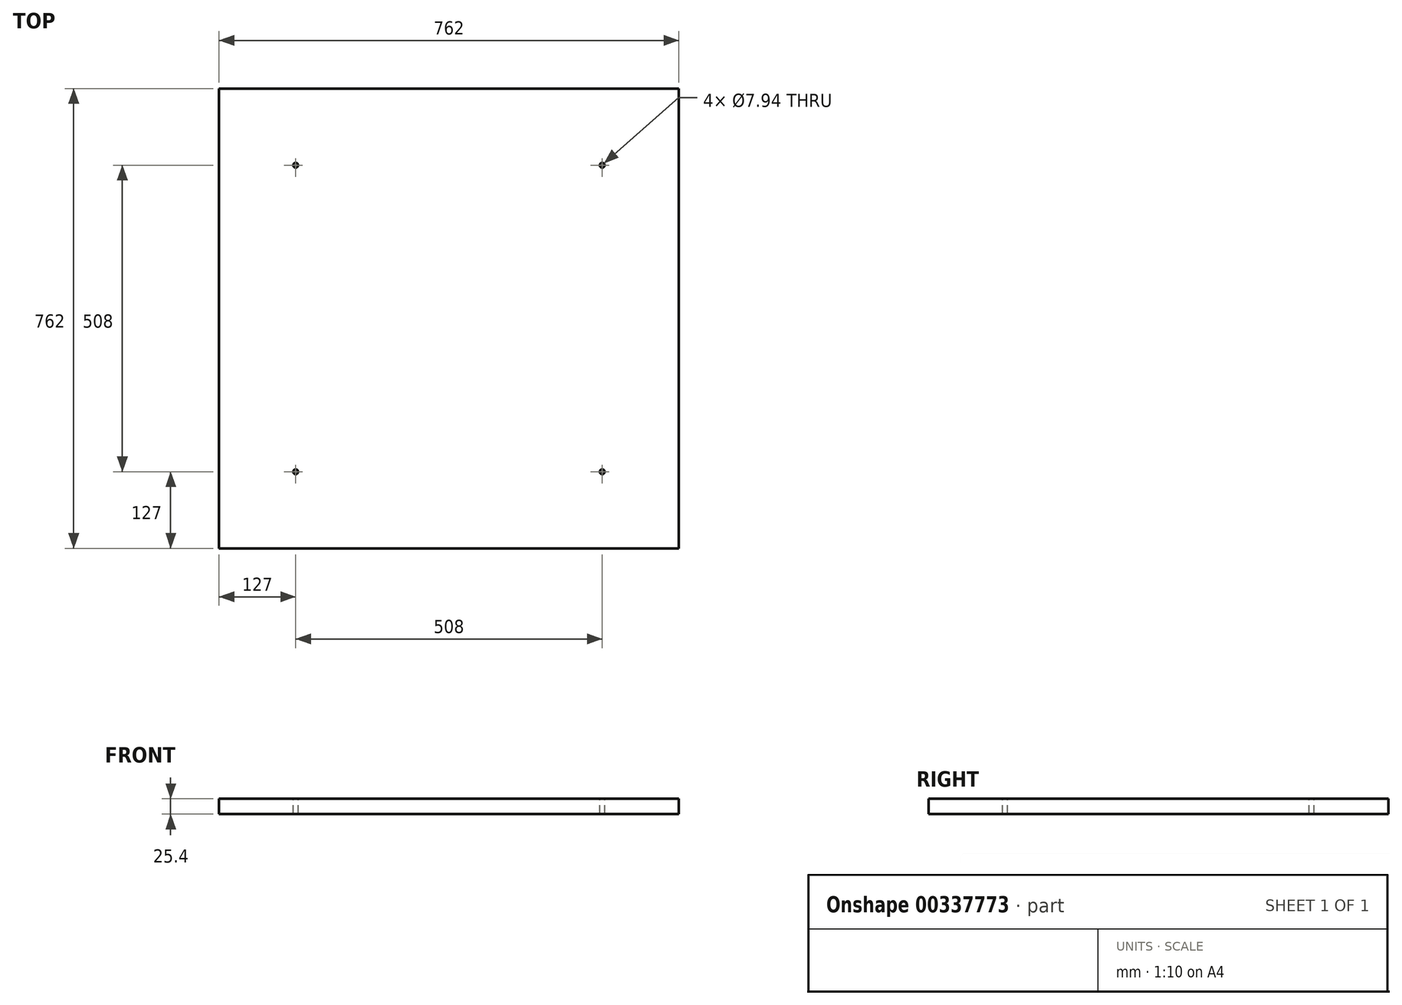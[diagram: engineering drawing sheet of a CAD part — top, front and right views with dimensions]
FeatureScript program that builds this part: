
annotation { "Feature Type Name" : "Feature", "Feature Type Description" : "" }
export const myFeature = defineFeature(function(context is Context, id is Id, definition is map)
    precondition{}
    {
        {
            var Q0;
            Q0=qCreatedBy(makeId("Front.planeOp"),FACE);
            var sketch = newSketch(context, id + "F0", { "sketchPlane" : qUnion([Q0])});
            skLineSegment(sketch, "E0.bottom", {"start": v(0, 0) * mm, "end": v(762, 0) * mm});
            skLineSegment(sketch, "E0.top", {"start": v(0, 25.4) * mm, "end": v(762, 25.4) * mm});
            skLineSegment(sketch, "E0.left", {"start": v(0, 0) * mm, "end": v(0, 25.4) * mm});
            skLineSegment(sketch, "E0.right", {"start": v(762, 0) * mm, "end": v(762, 25.4) * mm});
            skSolve(sketch);
        }
        {
            var Q0;
            Q0 = qSketchRegion(id + "F0", true);
            extrude(context, id + "F1", {"entities" : qUnion([Q0]), "oppositeDirection" : true, "depth" : 762 * mm});
        }
        {
            var Q0;
            Q0=makeQuery(id+"F1.opExtrude","SWEPT_FACE",FACE,{"disambiguationData":[OSD([sQuery(id+"F0.wireOp",EDGE,"E0.top")])]});
            var sketch = newSketch(context, id + "F2", { "sketchPlane" : qUnion([Q0])});
            skLineSegment(sketch, "E1.bottom", {"start": v(635, 635) * mm, "end": v(127, 635) * mm});
            skLineSegment(sketch, "E1.top", {"start": v(635, 127) * mm, "end": v(127, 127) * mm});
            skLineSegment(sketch, "E1.left", {"start": v(635, 635) * mm, "end": v(635, 127) * mm});
            skLineSegment(sketch, "E1.right", {"start": v(127, 635) * mm, "end": v(127, 127) * mm});
            skSolve(sketch);
        }
        {
            var Q0;
            Q0=sQuery(id+"F2.wireOp",VERTEX,"E1.left.end");
            var Q1;
            Q1=sQuery(id+"F2.wireOp",VERTEX,"E1.left.start");
            var Q2;
            Q2=sQuery(id+"F2.wireOp",VERTEX,"E1.top.end");
            var Q3;
            Q3=sQuery(id+"F2.wireOp",VERTEX,"E1.right.start");
            var Q4;
            Q4=makeQuery(id+"F1.opExtrude","SWEPT_BODY",BODY,{"disambiguationData":[OSD([sQuery(id+"F0.wireOp",EDGE,"E0.bottom"),sQuery(id+"F0.wireOp",EDGE,"E0.top"),sQuery(id+"F0.wireOp",EDGE,"E0.left"),sQuery(id+"F0.wireOp",EDGE,"E0.right")])]});
            hole(context, id + "F3", {"style" : HoleStyle.SIMPLE, "endStyle" : HoleEndStyle.THROUGH, "standardTappedOrClearance" : lookupTablePath({ "standard" : "ANSI", "engagement" : "75%", "pitch" : "16 tpi", "size" : "3/8", "type" : "Tapped" }), "standardBlindInLast" : lookupTablePath({ "standard" : "ANSI", "engagement" : "75%", "pitch" : "16 tpi", "size" : "3/8", "type" : "Tapped" }), "holeDiameter" : 7.94 * mm, "showTappedDepth" : true, "tappedDepth" : 12.7 * mm, "tapClearance" : 3, "locations" : qUnion([Q0, Q1, Q2, Q3]), "scope" : qUnion([Q4]), "majorDiameter" : 9.53 * mm});
        }
    });
